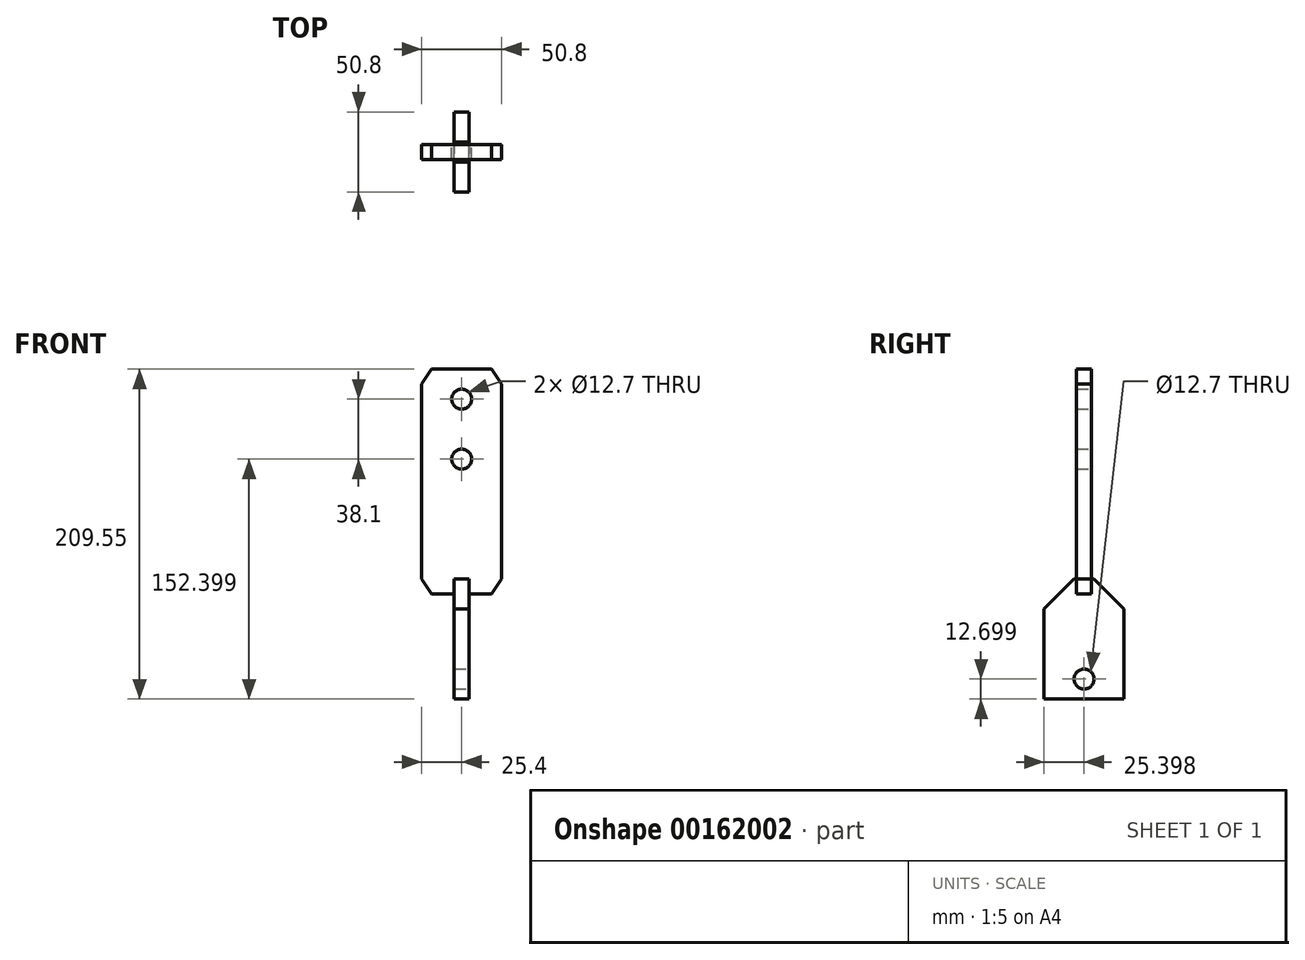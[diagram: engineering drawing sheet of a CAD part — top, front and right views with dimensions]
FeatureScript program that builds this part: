
annotation { "Feature Type Name" : "Feature", "Feature Type Description" : "" }
export const myFeature = defineFeature(function(context is Context, id is Id, definition is map)
    precondition{}
    {
        {
            var Q0;
            Q0=qCreatedBy(makeId("Front.planeOp"),FACE);
            var sketch = newSketch(context, id + "F0", { "sketchPlane" : qUnion([Q0])});
            skLineSegment(sketch, "E0", {"start": v(-25.4, 137.67) * mm, "end": v(-25.4, 75.76) * mm});
            skLineSegment(sketch, "E1", {"start": v(25.4, 75.76) * mm, "end": v(25.4, 137.67) * mm});
            skLineSegment(sketch, "E2", {"start": v(-19.05, 147.19) * mm, "end": v(-25.4, 137.67) * mm});
            skLineSegment(sketch, "E3.MirrorCS", {"start": v(19.05, 147.19) * mm, "end": v(25.4, 137.67) * mm});
            skLineSegment(sketch, "E4", {"start": v(-19.05, 147.19) * mm, "end": v(19.05, 147.19) * mm});
            skLineSegment(sketch, "E5.MirrorCS", {"start": v(25.4, 75.76) * mm, "end": v(25.4, 13.84) * mm});
            skLineSegment(sketch, "E6.MirrorCS", {"start": v(19.05, 4.32) * mm, "end": v(25.4, 13.84) * mm});
            skLineSegment(sketch, "E7.MirrorCS", {"start": v(-19.05, 4.32) * mm, "end": v(-25.4, 13.84) * mm});
            skLineSegment(sketch, "E8.MirrorCS", {"start": v(-25.4, 13.84) * mm, "end": v(-25.4, 75.76) * mm});
            skPoint(sketch, "E9.endSnap0", {"position": v(0, 147.19) * mm});
            skCircle(sketch, "E10", {"center": v(0, 128.14) * mm, "radius": 6.35 * mm});
            skCircle(sketch, "E11", {"center": v(0, 90.04) * mm, "radius": 6.35 * mm});
            skLineSegment(sketch, "E12", {"start": v(-19.05, 4.32) * mm, "end": v(19.05, 4.32) * mm});
            skSolve(sketch);
        }
        {
            var Q0;
            Q0=makeQuery(id+"F0.imprint","IMPRINT",FACE,{"disambiguationData":[TD([[makeQuery(id+"F0.imprint","IMPRINT",EDGE,{"derivedFrom":sQuery(id+"F0.wireOp",EDGE,"E0")}),1.0]])]});
            extrude(context, id + "F1", {"entities" : qUnion([Q0]), "depth" : 9.52 * mm});
        }
        {
            var Q0;
            Q0=makeQuery(id+"F1.opExtrude","SWEPT_FACE",FACE,{"disambiguationData":[OSD([sQuery(id+"F0.wireOp",EDGE,"E1"),sQuery(id+"F0.wireOp",EDGE,"E5.MirrorCS")])]});
            var sketch = newSketch(context, id + "F2", { "sketchPlane" : qUnion([Q0])});
            skLineSegment(sketch, "E13", {"start": v(-11.11, 13.84) * mm, "end": v(1.59, 13.84) * mm});
            skLineSegment(sketch, "E14", {"start": v(-30.16, -5.21) * mm, "end": v(-30.16, -62.36) * mm});
            skLineSegment(sketch, "E15", {"start": v(-30.16, -62.36) * mm, "end": v(20.64, -62.36) * mm});
            skLineSegment(sketch, "E16", {"start": v(20.64, -62.36) * mm, "end": v(20.64, -5.21) * mm});
            skLineSegment(sketch, "E17", {"start": v(-30.16, -5.21) * mm, "end": v(-11.11, 13.84) * mm});
            skLineSegment(sketch, "E18.MirrorCS", {"start": v(20.64, -5.21) * mm, "end": v(1.59, 13.84) * mm});
            skCircle(sketch, "E19", {"center": v(-4.76, -49.66) * mm, "radius": 6.35 * mm});
            skSolve(sketch);
        }
        {
            var Q0;
            Q0=makeQuery(id+"F2.imprint","IMPRINT",FACE,{"disambiguationData":[TD([[makeQuery(id+"F2.imprint","IMPRINT",EDGE,{"derivedFrom":sQuery(id+"F2.wireOp",EDGE,"E14")}),1.0]])]});
            extrude(context, id + "F3", {"entities" : qUnion([Q0]), "operationType" : NewBodyOperationType.ADD, "oppositeDirection" : true, "depth" : 30.16 * mm, "hasSecondDirection" : true, "secondDirectionOppositeDirection" : true, "secondDirectionDepth" : 20.64 * mm});
        }
    });
